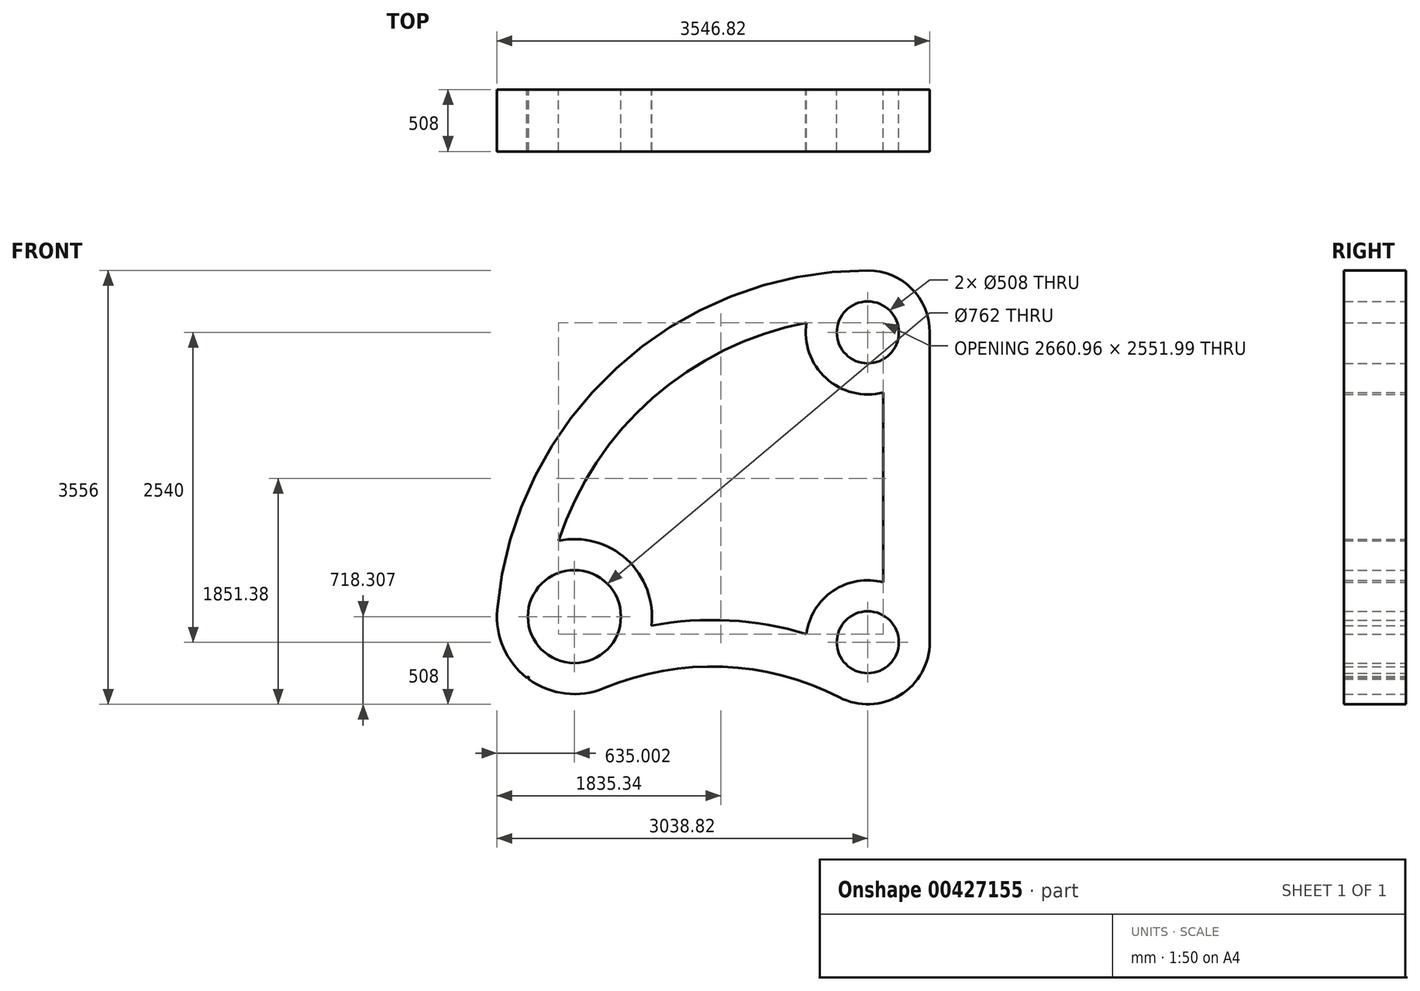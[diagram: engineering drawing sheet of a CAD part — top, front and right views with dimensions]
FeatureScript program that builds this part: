
annotation { "Feature Type Name" : "Feature", "Feature Type Description" : "" }
export const myFeature = defineFeature(function(context is Context, id is Id, definition is map)
    precondition{}
    {
        {
            var Q0;
            Q0=qCreatedBy(makeId("Front.planeOp"),FACE);
            var sketch = newSketch(context, id + "F0", { "sketchPlane" : qUnion([Q0])});
            skCircle(sketch, "E0", {"center": v(0, 0) * mm, "radius": 254 * mm});
            skArc(sketch, "E1", {"start": v(-232.28, -451.79) * mm, "mid": v(264.64, -433.63) * mm, "end": v(508, 0) * mm});
            skCircle(sketch, "E2", {"center": v(0, 2540) * mm, "radius": 254 * mm});
            skArc(sketch, "E3", {"start": v(508, 2540) * mm, "mid": v(359.21, 2899.21) * mm, "end": v(0, 3048) * mm});
            skLineSegment(sketch, "E4", {"start": v(508, 0) * mm, "end": v(508, 2540) * mm});
            skArc(sketch, "E5", {"start": v(-2779.82, -281.18) * mm, "mid": v(-2778.69, -292.14) * mm, "end": v(-2777.51, -303.1) * mm});
            skCircle(sketch, "E6", {"center": v(-2403.82, 210.3) * mm, "radius": 381 * mm});
            skArc(sketch, "E7", {"start": v(-3036.4, 265.65) * mm, "mid": v(-2778.5, -302.37) * mm, "end": v(-2158.97, -375.6) * mm});
            skArc(sketch, "E8.0", {"start": v(-503.51, 67.39) * mm, "mid": v(-1134.23, 178.32) * mm, "end": v(-1773.21, 135.7) * mm});
            skLineSegment(sketch, "E9.trimOffspring", {"start": v(127, 491.87) * mm, "end": v(127, 2048.13) * mm});
            skArc(sketch, "E10.trimOffspring", {"start": v(-2779.82, -281.18) * mm, "mid": v(-2786.83, -285.98) * mm, "end": v(-2793.83, -290.8) * mm});
            skArc(sketch, "E11.trimOffspring", {"start": v(-1773.21, 135.7) * mm, "mid": v(-1975.14, 678.78) * mm, "end": v(-2533.96, 831.83) * mm});
            skArc(sketch, "E12.trimOffspring", {"start": v(-232.28, -451.79) * mm, "mid": v(-1187.2, -200.6) * mm, "end": v(-2158.97, -375.6) * mm});
            skArc(sketch, "E13.trimOffspring", {"start": v(0, 3048) * mm, "mid": v(-2059.2, 2247.22) * mm, "end": v(-3036.4, 265.65) * mm});
            skArc(sketch, "E14.trimOffspring", {"start": v(-501.76, 2619.38) * mm, "mid": v(-1761.46, 2002.54) * mm, "end": v(-2533.96, 831.83) * mm});
            skArc(sketch, "E15.trimOffspring", {"start": v(127, 491.87) * mm, "mid": v(-283.7, 421.4) * mm, "end": v(-503.51, 67.39) * mm});
            skArc(sketch, "E16.trimOffspring", {"start": v(-501.76, 2619.38) * mm, "mid": v(-341.6, 2164) * mm, "end": v(127, 2048.13) * mm});
            skSolve(sketch);
        }
        {
            var Q0;
            Q0=makeQuery(id+"F0.imprint","IMPRINT",FACE,{"disambiguationData":[TD([[makeQuery(id+"F0.imprint","IMPRINT",EDGE,{"derivedFrom":sQuery(id+"F0.wireOp",EDGE,"E0")}),-1.0]])]});
            extrude(context, id + "F1", {"entities" : qUnion([Q0]), "depth" : 508 * mm});
        }
    });
